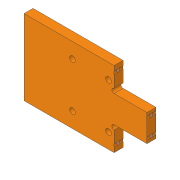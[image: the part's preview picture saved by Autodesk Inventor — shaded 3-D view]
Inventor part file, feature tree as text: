
AUTODESK INVENTOR PART (.ipt)
format: ipt  version: 2019.4 (Build 234330000, 330)  size: 155,136 bytes
history: native  units: mm
features: sketch x3, hole x3, other x1, extrude x1
ambient origin geometry x8: Origin, YZ Plane, XZ Plane, XY Plane, X Axis, Y Axis, Z Axis, Center Point
bodies: Body1 (feature_tree)
feature tree (8):
  other  "ソリッド1"
  sketch  "スケッチ1"
  extrude  "押し出し1"  Depth=20.0mm
  hole  "穴1"  [1 undecoded]
  hole  "穴2"  [1 undecoded]
  hole  "穴3"  [1 undecoded]
  sketch  "スケッチ2"
  sketch  "スケッチ3"
note: 3 required parameter values undecoded (feature->parameter linkage not recoverable at this tier; creation-order binding heuristic only, values carry confidence <= 0.55)
